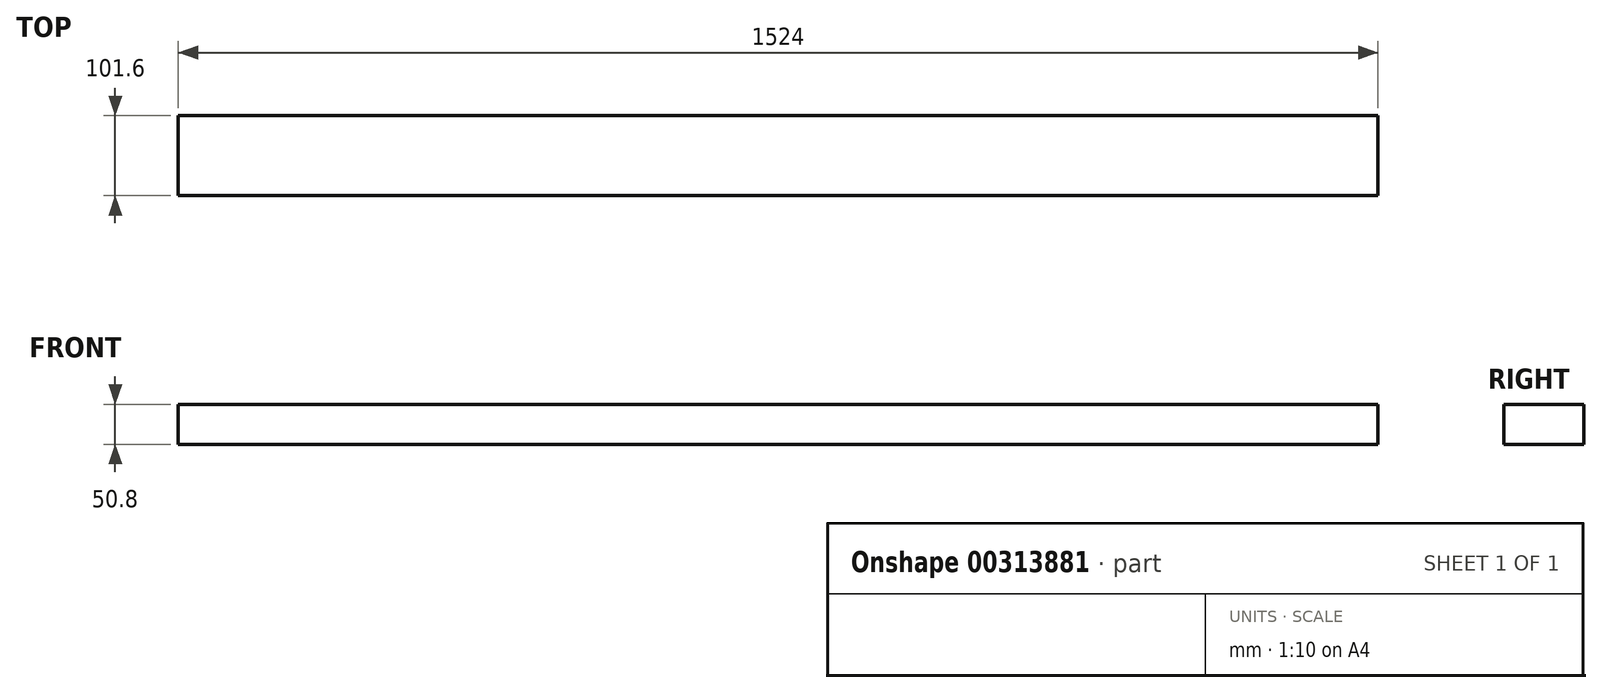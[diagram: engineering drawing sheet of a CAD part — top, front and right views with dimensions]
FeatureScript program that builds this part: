
annotation { "Feature Type Name" : "Feature", "Feature Type Description" : "" }
export const myFeature = defineFeature(function(context is Context, id is Id, definition is map)
    precondition{}
    {
        {
            var Q0;
            Q0=qCreatedBy(makeId("Top.planeOp"),FACE);
            var sketch = newSketch(context, id + "F0", { "sketchPlane" : qUnion([Q0])});
            skLineSegment(sketch, "E0", {"start": v(-777.76, 101.6) * mm, "end": v(746.24, 101.6) * mm});
            skLineSegment(sketch, "E1", {"start": v(-777.76, 101.6) * mm, "end": v(-777.76, 0) * mm});
            skLineSegment(sketch, "E2", {"start": v(-777.76, 0) * mm, "end": v(746.24, 0) * mm});
            skLineSegment(sketch, "E3", {"start": v(746.24, 0) * mm, "end": v(746.24, 101.6) * mm});
            skSolve(sketch);
        }
        {
            var Q0;
            Q0=makeQuery(id+"F0.imprint","IMPRINT",FACE,{"disambiguationData":[TD([[makeQuery(id+"F0.imprint","IMPRINT",EDGE,{"derivedFrom":sQuery(id+"F0.wireOp",EDGE,"E0")}),-1.0]])]});
            extrude(context, id + "F1", {"entities" : qUnion([Q0]), "depth" : 50.8 * mm});
        }
    });
